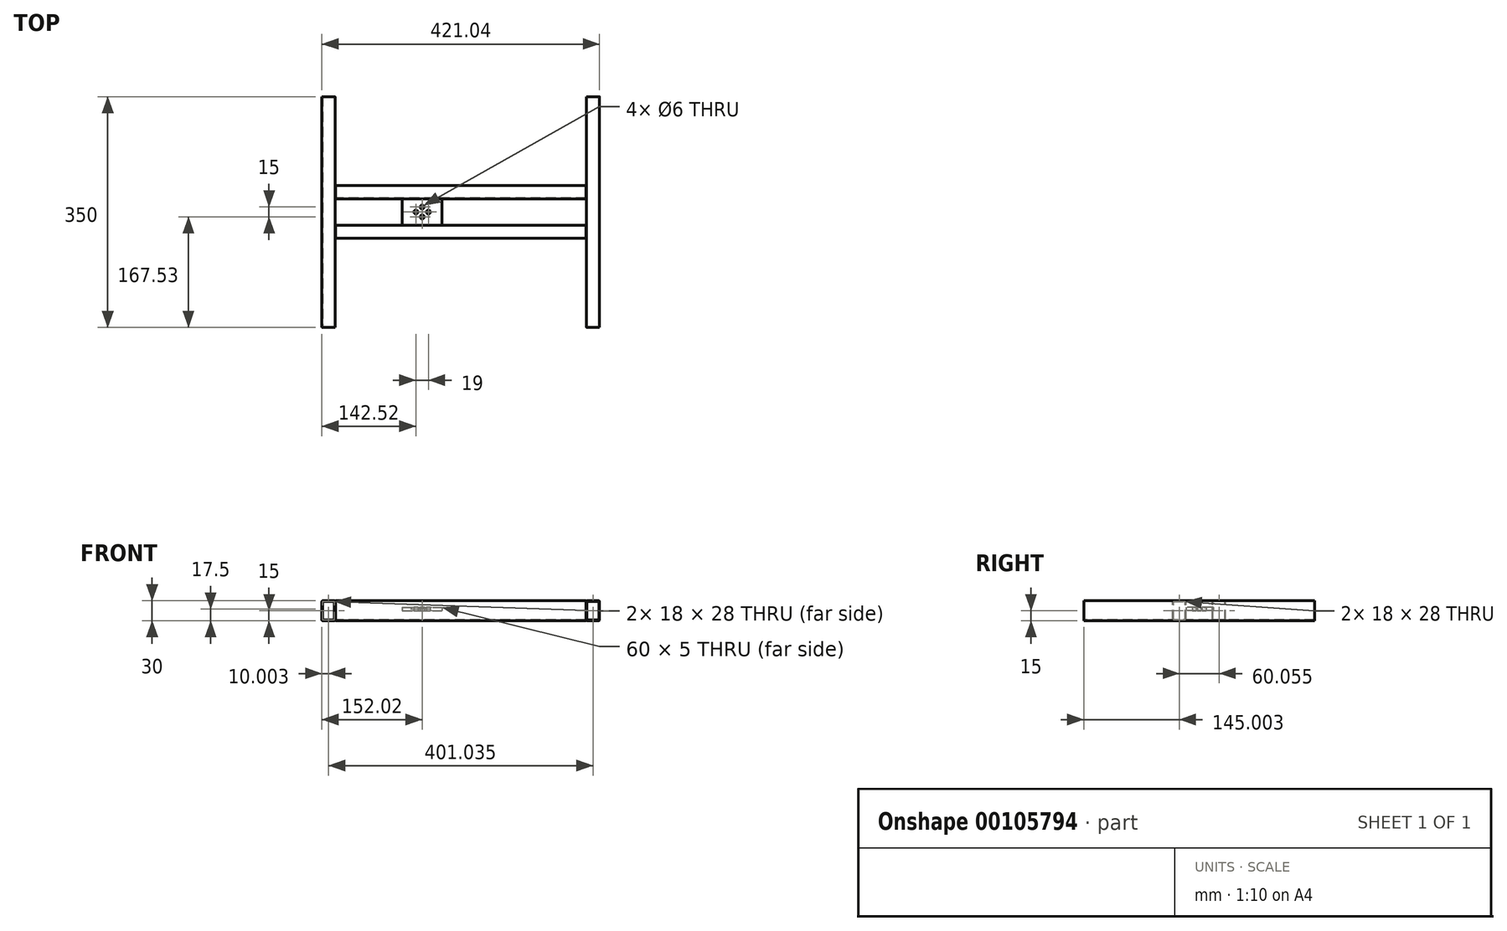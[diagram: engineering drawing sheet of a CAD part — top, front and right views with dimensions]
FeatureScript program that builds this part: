
annotation { "Feature Type Name" : "Feature", "Feature Type Description" : "" }
export const myFeature = defineFeature(function(context is Context, id is Id, definition is map)
    precondition{}
    {
        {
            var Q0;
            Q0=qCreatedBy(makeId("Front.planeOp"),FACE);
            cPlane(context, id + "F0", {"entities" : qUnion([Q0]), "cplaneType" : CPlaneType.OFFSET, "offset" : 175 * mm, "width" : 150 * mm, "height" : 150 * mm});
        }
        {
            var Q0;
            Q0=qCreatedBy(makeId("Top.planeOp"),FACE);
            var sketch = newSketch(context, id + "F1", { "sketchPlane" : qUnion([Q0])});
            skLineSegment(sketch, "E0", {"start": v(-200.52, 174.97) * mm, "end": v(-200.52, -175.03) * mm});
            skLineSegment(sketch, "E1", {"start": v(-200.52, -0.03) * mm, "end": v(370.75, -0.03) * mm, "construction": true});
            skPoint(sketch, "E1.endSnap0", {"position": v(-200.52, -0.03) * mm});
            skLineSegment(sketch, "E2", {"start": v(-200.52, 29.97) * mm, "end": v(199.48, 29.97) * mm, "construction": true});
            skLineSegment(sketch, "E3", {"start": v(-200.52, -30.03) * mm, "end": v(199.48, -30.03) * mm, "construction": true});
            skPoint(sketch, "E4.endSnap0", {"position": v(-0.52, -30.03) * mm});
            skLineSegment(sketch, "E5", {"start": v(-200.52, 174.97) * mm, "end": v(199.48, 174.97) * mm, "construction": true});
            skLineSegment(sketch, "E6", {"start": v(-200.52, -175.03) * mm, "end": v(212.72, -175.03) * mm, "construction": true});
            skLineSegment(sketch, "E7", {"start": v(199.48, 174.97) * mm, "end": v(199.48, -175.03) * mm});
            skPoint(sketch, "E8", {"position": v(-190.52, 29.97) * mm});
            skPoint(sketch, "E9", {"position": v(-190.52, -30.03) * mm});
            skLineSegment(sketch, "E10", {"start": v(-190.52, 29.97) * mm, "end": v(189.48, 29.97) * mm});
            skLineSegment(sketch, "E11", {"start": v(-190.52, -30.03) * mm, "end": v(189.48, -30.03) * mm});
            skSolve(sketch);
        }
        {
            var Q0;
            Q0=qCreatedBy(id+"F0.planeOp",FACE);
            var sketch = newSketch(context, id + "F2", { "sketchPlane" : qUnion([Q0])});
            skLineSegment(sketch, "E12.bottom", {"start": v(-191.52, -15) * mm, "end": v(-209.52, -15) * mm});
            skLineSegment(sketch, "E12.top", {"start": v(-191.52, 15) * mm, "end": v(-209.52, 15) * mm});
            skLineSegment(sketch, "E12.left", {"start": v(-190.52, -14) * mm, "end": v(-190.52, 14) * mm});
            skLineSegment(sketch, "E12.right", {"start": v(-210.52, -14) * mm, "end": v(-210.52, 14) * mm});
            skPoint(sketch, "E12.middle", {"position": v(-200.52, 0) * mm});
            skPoint(sketch, "E13.visualSharp", {"position": v(-190.52, 15) * mm});
            skArc(sketch, "E13.filletArc", {"start": v(-190.52, 14) * mm, "mid": v(-190.81, 14.7) * mm, "end": v(-191.52, 15) * mm});
            skPoint(sketch, "E14.visualSharp", {"position": v(-210.52, 15) * mm});
            skArc(sketch, "E14.filletArc", {"start": v(-209.52, 15) * mm, "mid": v(-210.22, 14.7) * mm, "end": v(-210.52, 14) * mm});
            skPoint(sketch, "E15.visualSharp", {"position": v(-210.52, -15) * mm});
            skArc(sketch, "E15.filletArc", {"start": v(-210.52, -14) * mm, "mid": v(-210.22, -14.7) * mm, "end": v(-209.52, -15) * mm});
            skPoint(sketch, "E16.visualSharp", {"position": v(-190.52, -15) * mm});
            skArc(sketch, "E16.filletArc", {"start": v(-191.52, -15) * mm, "mid": v(-190.81, -14.7) * mm, "end": v(-190.52, -14) * mm});
            skLineSegment(sketch, "E17.0", {"start": v(-191.52, -14) * mm, "end": v(-209.52, -14) * mm});
            skLineSegment(sketch, "E17.1", {"start": v(-191.52, -14) * mm, "end": v(-191.52, 14) * mm});
            skLineSegment(sketch, "E17.2", {"start": v(-191.52, 14) * mm, "end": v(-209.52, 14) * mm});
            skLineSegment(sketch, "E17.3", {"start": v(-209.52, -14) * mm, "end": v(-209.52, 14) * mm});
            skArc(sketch, "E18.MirrorCS", {"start": v(191.52, -15) * mm, "mid": v(190.81, -14.7) * mm, "end": v(190.52, -14) * mm});
            skArc(sketch, "E19.MirrorCS", {"start": v(190.52, 14) * mm, "mid": v(190.81, 14.7) * mm, "end": v(191.52, 15) * mm});
            skArc(sketch, "E20.MirrorCS", {"start": v(210.52, -14) * mm, "mid": v(210.22, -14.7) * mm, "end": v(209.52, -15) * mm});
            skArc(sketch, "E21.MirrorCS", {"start": v(209.52, 15) * mm, "mid": v(210.22, 14.7) * mm, "end": v(210.52, 14) * mm});
            skLineSegment(sketch, "E22.MirrorCS", {"start": v(191.52, -15) * mm, "end": v(209.52, -15) * mm});
            skLineSegment(sketch, "E23.MirrorCS", {"start": v(191.52, -14) * mm, "end": v(209.52, -14) * mm});
            skLineSegment(sketch, "E24.MirrorCS", {"start": v(190.52, -14) * mm, "end": v(190.52, 14) * mm});
            skPoint(sketch, "E25.MirrorP", {"position": v(190.52, 15) * mm});
            skPoint(sketch, "E26.MirrorP", {"position": v(210.52, -15) * mm});
            skLineSegment(sketch, "E27.MirrorCS", {"start": v(210.52, -14) * mm, "end": v(210.52, 14) * mm});
            skPoint(sketch, "E28.MirrorP", {"position": v(210.52, 15) * mm});
            skLineSegment(sketch, "E29.MirrorCS", {"start": v(209.52, -14) * mm, "end": v(209.52, 14) * mm});
            skLineSegment(sketch, "E30.MirrorCS", {"start": v(191.52, -14) * mm, "end": v(191.52, 14) * mm});
            skLineSegment(sketch, "E31.MirrorCS", {"start": v(191.52, 14) * mm, "end": v(209.52, 14) * mm});
            skPoint(sketch, "E32.MirrorP", {"position": v(200.52, 0) * mm});
            skPoint(sketch, "E33.MirrorP", {"position": v(190.52, -15) * mm});
            skLineSegment(sketch, "E34.MirrorCS", {"start": v(191.52, 15) * mm, "end": v(209.52, 15) * mm});
            skSolve(sketch);
        }
        {
            var Q0;
            Q0 = qSketchRegion(id + "F2", true);
            var Q1;
            Q1=sQuery(id+"F1.wireOp",EDGE,"E0");
            sweep(context, id + "F3", {"profiles" : qUnion([Q0]), "path" : qUnion([Q1])});
        }
        {
            var Q0;
            Q0=qCreatedBy(makeId("Right.planeOp"),FACE);
            cPlane(context, id + "F4", {"entities" : qUnion([Q0]), "cplaneType" : CPlaneType.OFFSET, "offset" : 190 * mm, "width" : 150 * mm, "height" : 150 * mm});
        }
        {
            var Q0;
            Q0=qCreatedBy(id+"F4.planeOp",FACE);
            var sketch = newSketch(context, id + "F5", { "sketchPlane" : qUnion([Q0])});
            skLineSegment(sketch, "E35.bottom", {"start": v(-39.03, -15) * mm, "end": v(-21.03, -15) * mm});
            skLineSegment(sketch, "E35.top", {"start": v(-39.03, 15) * mm, "end": v(-21.03, 15) * mm});
            skLineSegment(sketch, "E35.left", {"start": v(-40.03, -14) * mm, "end": v(-40.03, 14) * mm});
            skLineSegment(sketch, "E35.right", {"start": v(-20.03, -14) * mm, "end": v(-20.03, 14) * mm});
            skPoint(sketch, "E35.middle", {"position": v(-30.03, 0) * mm});
            skPoint(sketch, "E36.visualSharp", {"position": v(-20.03, -15) * mm});
            skArc(sketch, "E36.filletArc", {"start": v(-21.03, -15) * mm, "mid": v(-20.32, -14.7) * mm, "end": v(-20.03, -14) * mm});
            skPoint(sketch, "E37.visualSharp", {"position": v(-40.03, -15) * mm});
            skArc(sketch, "E37.filletArc", {"start": v(-40.03, -14) * mm, "mid": v(-39.73, -14.7) * mm, "end": v(-39.03, -15) * mm});
            skPoint(sketch, "E38.visualSharp", {"position": v(-20.03, 15) * mm});
            skArc(sketch, "E38.filletArc", {"start": v(-20.03, 14) * mm, "mid": v(-20.32, 14.7) * mm, "end": v(-21.03, 15) * mm});
            skPoint(sketch, "E39.visualSharp", {"position": v(-40.03, 15) * mm});
            skArc(sketch, "E39.filletArc", {"start": v(-39.03, 15) * mm, "mid": v(-39.73, 14.7) * mm, "end": v(-40.03, 14) * mm});
            skLineSegment(sketch, "E40.0", {"start": v(-39.03, -14) * mm, "end": v(-39.03, 14) * mm});
            skLineSegment(sketch, "E40.1", {"start": v(-39.03, -14) * mm, "end": v(-21.03, -14) * mm});
            skLineSegment(sketch, "E40.2", {"start": v(-21.03, -14) * mm, "end": v(-21.03, 14) * mm});
            skLineSegment(sketch, "E40.3", {"start": v(-39.03, 14) * mm, "end": v(-21.03, 14) * mm});
            skArc(sketch, "E41.MirrorCS", {"start": v(21.03, -15) * mm, "mid": v(20.32, -14.7) * mm, "end": v(20.03, -14) * mm});
            skArc(sketch, "E42.MirrorCS", {"start": v(40.03, -14) * mm, "mid": v(39.73, -14.7) * mm, "end": v(39.03, -15) * mm});
            skArc(sketch, "E43.MirrorCS", {"start": v(20.03, 14) * mm, "mid": v(20.32, 14.7) * mm, "end": v(21.03, 15) * mm});
            skArc(sketch, "E44.MirrorCS", {"start": v(39.03, 15) * mm, "mid": v(39.73, 14.7) * mm, "end": v(40.03, 14) * mm});
            skLineSegment(sketch, "E45.MirrorCS", {"start": v(39.03, -14) * mm, "end": v(21.03, -14) * mm});
            skPoint(sketch, "E46.MirrorP", {"position": v(20.03, 15) * mm});
            skPoint(sketch, "E47.MirrorP", {"position": v(20.03, -15) * mm});
            skPoint(sketch, "E48.MirrorP", {"position": v(40.03, -15) * mm});
            skLineSegment(sketch, "E49.MirrorCS", {"start": v(40.03, -14) * mm, "end": v(40.03, 14) * mm});
            skLineSegment(sketch, "E50.MirrorCS", {"start": v(20.03, -14) * mm, "end": v(20.03, 14) * mm});
            skPoint(sketch, "E51.MirrorP", {"position": v(30.03, 0) * mm});
            skLineSegment(sketch, "E52.MirrorCS", {"start": v(39.03, 14) * mm, "end": v(21.03, 14) * mm});
            skPoint(sketch, "E53.MirrorP", {"position": v(40.03, 15) * mm});
            skLineSegment(sketch, "E54.MirrorCS", {"start": v(39.03, 15) * mm, "end": v(21.03, 15) * mm});
            skLineSegment(sketch, "E55.MirrorCS", {"start": v(39.03, -15) * mm, "end": v(21.03, -15) * mm});
            skLineSegment(sketch, "E56.MirrorCS", {"start": v(39.03, -14) * mm, "end": v(39.03, 14) * mm});
            skLineSegment(sketch, "E57.MirrorCS", {"start": v(21.03, -14) * mm, "end": v(21.03, 14) * mm});
            skSolve(sketch);
        }
        {
            var Q0;
            Q0 = qSketchRegion(id + "F5", true);
            var Q1;
            Q1=sQuery(id+"F1.wireOp",EDGE,"E11");
            sweep(context, id + "F6", {"profiles" : qUnion([Q0]), "path" : qUnion([Q1])});
        }
        {
            var Q0;
            Q0=qCreatedBy(makeId("Top.planeOp"),FACE);
            var sketch = newSketch(context, id + "F7", { "sketchPlane" : qUnion([Q0])});
            skLineSegment(sketch, "E58.bottom", {"start": v(-88.5, 21.19) * mm, "end": v(-28.5, 21.19) * mm});
            skLineSegment(sketch, "E58.top", {"start": v(-88.5, -20.68) * mm, "end": v(-28.5, -20.68) * mm});
            skLineSegment(sketch, "E58.left", {"start": v(-88.5, 21.19) * mm, "end": v(-88.5, -20.68) * mm});
            skLineSegment(sketch, "E58.right", {"start": v(-28.5, 21.19) * mm, "end": v(-28.5, -20.68) * mm});
            skPoint(sketch, "E59", {"position": v(-68, 0) * mm});
            skPoint(sketch, "E60", {"position": v(-49, 0) * mm});
            skLineSegment(sketch, "E61", {"start": v(-68, 0) * mm, "end": v(-49, 0) * mm, "construction": true});
            skLineSegment(sketch, "E62", {"start": v(-58.5, 0) * mm, "end": v(-58.5, -10.41) * mm, "construction": true});
            skLineSegment(sketch, "E63", {"start": v(-58.5, 0) * mm, "end": v(-58.5, 9.84) * mm, "construction": true});
            skPoint(sketch, "E64", {"position": v(-58.5, -7.5) * mm});
            skPoint(sketch, "E65", {"position": v(-58.5, 7.5) * mm});
            skLineSegment(sketch, "E66", {"start": v(-58.5, -10.41) * mm, "end": v(-58.5, -20.68) * mm, "construction": true});
            skSolve(sketch);
        }
        {
            var Q0;
            Q0=makeQuery(id+"F7.imprint","IMPRINT",FACE,{"disambiguationData":[TD([[makeQuery(id+"F7.imprint","IMPRINT",EDGE,{"derivedFrom":sQuery(id+"F7.wireOp",EDGE,"E58.bottom")}),-1.0]])]});
            extrude(context, id + "F8", {"entities" : qUnion([Q0]), "operationType" : NewBodyOperationType.ADD, "depth" : 5 * mm});
        }
        {
            var Q0;
            Q0=sQuery(id+"F7.wireOp",VERTEX,"E64");
            var Q1;
            Q1=sQuery(id+"F7.wireOp",VERTEX,"E59");
            var Q2;
            Q2=sQuery(id+"F7.wireOp",VERTEX,"E65");
            var Q3;
            Q3=sQuery(id+"F7.wireOp",VERTEX,"E60");
            var Q4;
            Q4=makeQuery(id+"F6.opSweep","SWEPT_BODY",BODY,{"disambiguationData":[OSD([sQuery(id+"F1.wireOp",EDGE,"E3"),sQuery(id+"F5.wireOp",EDGE,"E35.bottom"),sQuery(id+"F5.wireOp",EDGE,"E35.top"),sQuery(id+"F5.wireOp",EDGE,"E35.left"),sQuery(id+"F5.wireOp",EDGE,"E35.right"),sQuery(id+"F5.wireOp",EDGE,"E36.filletArc"),sQuery(id+"F5.wireOp",EDGE,"E37.filletArc"),sQuery(id+"F5.wireOp",EDGE,"E38.filletArc"),sQuery(id+"F5.wireOp",EDGE,"E39.filletArc"),sQuery(id+"F5.wireOp",EDGE,"E40.0"),sQuery(id+"F5.wireOp",EDGE,"E40.1"),sQuery(id+"F5.wireOp",EDGE,"E40.2"),sQuery(id+"F5.wireOp",EDGE,"E40.3")])]});
            hole(context, id + "F9", {"style" : HoleStyle.SIMPLE, "endStyle" : HoleEndStyle.BLIND, "oppositeDirection" : true, "holeDiameter" : 6 * mm, "holeDepth" : 10 * mm, "locations" : qUnion([Q0, Q1, Q2, Q3]), "scope" : qUnion([Q4])});
        }
    });
